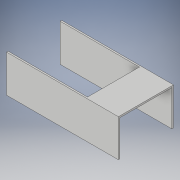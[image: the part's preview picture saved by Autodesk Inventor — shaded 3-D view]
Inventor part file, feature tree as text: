
AUTODESK INVENTOR PART (.ipt)
format: ipt  version: 2017 (Build 210142000, 142)  size: 131,584 bytes
history: native  units: in
note: dims shown in document units (in); Inventor stores cm internally (conversion verified against a paired STEP export)
features: extrude x6, sketch x6
ambient origin geometry x8: Origin, YZ Plane, XZ Plane, XY Plane, X Axis, Y Axis, Z Axis, Center Point
bodies: Solid1 (feature_tree)
feature tree (12):
  extrude  "Extrusion1"  Depth=5.75in
  extrude  "Extrusion2"  Depth=5.0in
  extrude  "Extrusion3"  Depth=8.0in TaperAngle=0.0deg
  extrude  "Extrusion4"  Depth=5.5in TaperAngle=0.0deg
  extrude  "Extrusion5"  Depth=13.5in TaperAngle=0.0deg
  extrude  "Extrusion6"  [1 undecoded]
  sketch  "Sketch1"  dims[d0=3.75in d1=5.75in]
  sketch  "Sketch2"  dims[d2=0.25in d3=0.0in d4=5.0in]
  sketch  "Sketch3"  dims[d5=0.25in d6=8.0in d7=0.0in]
  sketch  "Sketch4"  dims[d8=0.25in d9=0.0in d10=5.5in d11=0.0in]
  sketch  "Sketch5"  dims[d12=13.5in d13=0.0in d14=13.5in d15=0.0in]
  sketch  "Sketch6"
note: 1 required parameter value undecoded (feature->parameter linkage not recoverable at this tier; creation-order binding heuristic only, values carry confidence <= 0.55)
